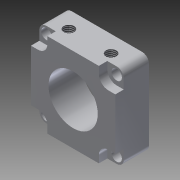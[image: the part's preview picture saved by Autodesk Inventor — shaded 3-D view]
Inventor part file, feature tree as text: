
AUTODESK INVENTOR PART (.ipt)
format: ipt  version: 2013 (Build 170138000, 138)  size: 196,096 bytes
history: native  units: in
note: dims shown in document units (in); Inventor stores cm internally (conversion verified against a paired STEP export)
features: extrude x4, thread x4, sketch x3, fillet x1
ambient origin geometry x8: Origin, YZ Plane, XZ Plane, XY Plane, X Axis, Y Axis, Z Axis, Center Point
bodies: Solid1 (feature_tree)
feature tree (12):
  sketch  "Sketch1"  dims[d0=1.5in d1=1.5in]
  extrude  "Extrusion1"  Depth=1.5in
  extrude  "Extrusion2"  Depth=0.7874in
  fillet  "Fillet1"  Radius=0.125in
  extrude  "Extrusion3"  Depth=0.75in
  extrude  "Extrusion4"  Depth=0.875in
  thread  "Thread1"  [1 undecoded]
  thread  "Thread2"  [1 undecoded]
  thread  "Thread3"  [1 undecoded]
  thread  "Thread4"  [1 undecoded]
  sketch  "Sketch2"  dims[d2=0.185in d3=0.7874in d5=1.25in d6=0.7874in d8=1.25in d11=0.125in]
  sketch  "Sketch3"  dims[d12=0.125in d13=0.75in d14=0.875in d15=0.5in d16=0.125in d17=0.125in d18=0.075in d22=1.5748in d24=360.0deg d26=0.15in d27=0.0in d28=0.45in d29=0.0in d30=0.125in d32=0.375in d33=0.375in d34=0.185in d35=0.185in d36=0.15in d37=0.0in d39=0.375in d40=0.375in d41=0.185in d42=0.185in d43=0.15in d44=0.0in d45=0.3in d46=0.3in d47=1.0in d48=0.0in d49=1.0in d50=0.0in d51=1.0in d52=0.0in d53=1.0in d54=0.0in]
note: 4 required parameter values undecoded (feature->parameter linkage not recoverable at this tier; creation-order binding heuristic only, values carry confidence <= 0.55)
